# Revit family: Grohe_BasinMixer_233242433
name_source: partatom
category: Plumbing Fixtures
units: mm (PartAtom-declared; Revit-internal decimal feet)

## family parameters
Cut with Voids When Loaded = No
Host = Face
OmniClass Number = 23.45.05.00
OmniClass Title = Sanitary Equipment
Part Type = Normal
Room Calculation Point = No
Round Connector Dimension = Use Diameter
Shared = No

## types (1)
- Basin Mixer (233242433)
    Assembly Code = D2013
    AssetType = Fixed
    BIMObjectName = Grohe_BasinMixer_233242433
    CO2NeutralProduction = GROHE is one of the first leading manufacturer within the sanitary industry having a CO2-neutral production.
    ClassificationName = Uniclass2015
    ClassificationValue = Pr_40_20_87_55
    Color = Grohe_Chrome
    Cost = 0 $
    Default Elevation = 0 mm  [stored 0 ft]
    Description = Basin Mixer
    DocumentationCertificates = https://www.bimstore.co
    DocumentationInstallationGuide = https://www.bimstore.co
    DocumentationLiterature = https://www.bimstore.co
    DocumentationMaintenance = https://www.bimstore.co
    DocumentationTechnical = https://www.bimstore.co
    DurationUnit = Years
    EF000003 = Top/tap hole
    EF000139 = Lacquered
    EF001707 = 0 °C
    EF002149 = FALSE
    EF002286 = Insert (push coupling)
    EF002671 = Black
    EF007955 = FALSE
    EF011775 = EB
    EF011779 = FALSE
    EF011781 = not applicable
    EF012753 = 0.00
    EF014578 = true
    EF014591 = false
    EF015280 = false
    EF016731 = Group I,<= 20 dB(A)
    EF020075 = Yes
    EF020105 = No
    EF020780 = Single-grip
    EF020781 = Plastic cartridge
    EF020785 = M26 x 1.5
    EF020787 = Group II, <=30 dB(A)
    EF020789 = 196
    EF020791 = Stainless steel
    EF020792 = FALSE
    EF020794 = FALSE
    EF020795 = Flexible with rinsing shower
    EF020796 = 228 mm  [stored 0.748031 ft]
    EF020797 = 121
    EF020798 = Waste unit
    EF020799 = TRUE
    EF020801 = FALSE
    EF021808 = 1-hole
    EF021835 = 0
    EF022042 = None
    EF022168 = FALSE
    EF022750 = Cast
    EF023686 = Other
    EF023687 = TRUE
    EF023688 = With hose connection
    EF025109 = Other
    EFDE0022 = None
    EFSE0002 = true
    Ecojoy = No
    ExpectedLife = 0
    Finish = Chrome
    FullRecyclabilityOfPlastic = All plastic components are fully recycable
    GROHESocialCommittment = green.grohe.com/social_engagement
    GROHESustainability = green.grohe.com
    IfcExportAs = IfcPipeFitting
    IfcExportType = IfcPipeFittingType
    Keynote = N16
    Manufacturer = Grohe
    ManufacturerName = Grohe
    Model = Basin Mixer
    ModelNumber = 233242433
    ModelReference = Basin Mixer
    NBSDescription = Mixer taps
    NBSObjectName = Grohe - Mixer taps
    NBSReference = 45-35-70/347
    NominalDepth = 0 mm  [stored 0 ft]
    NominalHeight = 0 mm  [stored 0 ft]
    NominalLength = 0 mm  [stored 0 ft]
    PQDiagramLink = https://cdn.cloud.grohe.com
    PrimaryMaterial = Grohe_Chrome
    ProductDescription = single hole installation

metal lever

GROHE SilkMove 28 mm ceramic cartridge

adjustable flow rate limiter

with temperature limiter

GROHE Long-Life finish

GROHE Water Saving mousseur 5.7 l/min

Lead and Nickel Free Inner Water Ways

GROHE FastFixation rapid installation system

smooth body

flexible connection hoses

professional exclusive
    ProductNumber = 233242433
    ProductShortText = Single-lever basin mixer 1/2"<br />M-Size
    ProductType = Single Lever Mixer
    ProductionYear = 2023
    SustainabilityAward = green.grohe.com/awards
    SustainabilityReport = green.grohe.com/reporting
    TPIDocumentLink = https://cdn.cloud.grohe.com
    Type Comments = Basin Mixer
    TypeName = Basin Mixer
    URL = https://www.grohe.co.uk
    WarrantyDurationLabor = 0
    WarrantyDurationParts = 0
    WarrantyDurationUnit = Years
    _BSBibleVersion = 17
    _BimSpecGuid = 0
    _CurrentRevision = 1
    _DistributedBy = https://www.bimstore.co
    _ObjectUserGuide = https://www.bimstore.co

note: [stored X ft] marks values corroborated as IEEE doubles in the binary element streams (Revit-internal decimal feet)

## geometry (parser evidence)
native form markers: Sweep x1
no freeform markers — native parametric forms only
